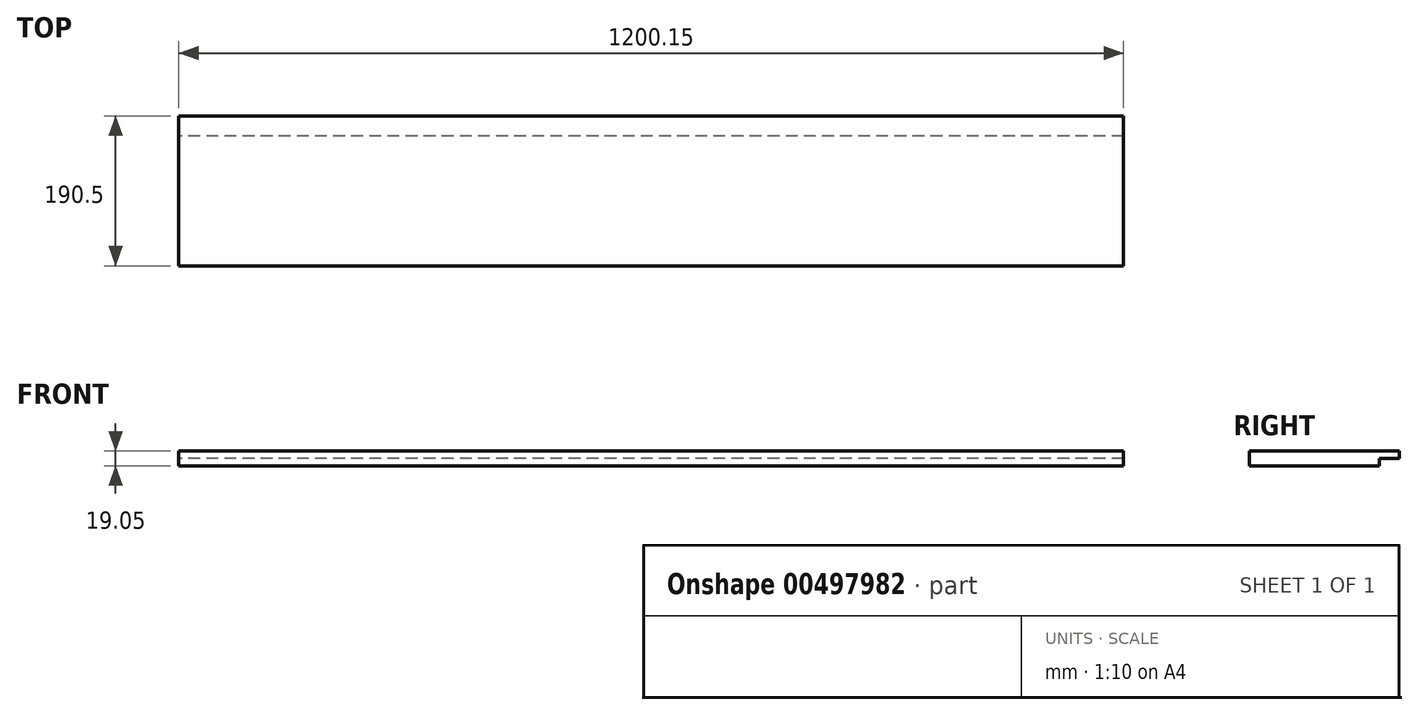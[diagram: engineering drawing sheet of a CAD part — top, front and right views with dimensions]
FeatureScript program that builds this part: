
annotation { "Feature Type Name" : "Feature", "Feature Type Description" : "" }
export const myFeature = defineFeature(function(context is Context, id is Id, definition is map)
    precondition{}
    {
        {
            var Q0;
            Q0=qCreatedBy(makeId("Right.planeOp"),FACE);
            var sketch = newSketch(context, id + "F0", { "sketchPlane" : qUnion([Q0])});
            skLineSegment(sketch, "E0.bottom", {"start": v(0, 0) * mm, "end": v(190.5, 0) * mm});
            skLineSegment(sketch, "E0.top", {"start": v(0, 19.05) * mm, "end": v(190.5, 19.05) * mm});
            skLineSegment(sketch, "E0.left", {"start": v(0, 0) * mm, "end": v(0, 19.05) * mm});
            skLineSegment(sketch, "E0.right", {"start": v(190.5, 0) * mm, "end": v(190.5, 19.05) * mm});
            skSolve(sketch);
        }
        {
            var Q0;
            Q0 = qSketchRegion(id + "F0", true);
            extrude(context, id + "F1", {"entities" : qUnion([Q0]), "depth" : 1200.15 * mm});
        }
        {
            var Q0;
            Q0=makeQuery(id+"F1.opExtrude","SWEPT_FACE",FACE,{"disambiguationData":[OSD([sQuery(id+"F0.wireOp",EDGE,"E0.right")])]});
            var sketch = newSketch(context, id + "F2", { "sketchPlane" : qUnion([Q0])});
            skLineSegment(sketch, "E1.0", {"start": v(-1200.15, 9.52) * mm, "end": v(0, 9.52) * mm});
            skSolve(sketch);
        }
        {
            var Q0;
            {var subQ0=sQuery(id+"F2.wireOp",EDGE,"E1.0");Q0=makeQuery(id+"F2.imprint","IMPRINT",FACE,{"disambiguationData":[TD([[makeQuery(id+"F2.imprint","IMPRINT",EDGE,{"derivedFrom":subQ0}),-1.0]])]});}
            extrude(context, id + "F3", {"entities" : qUnion([Q0]), "operationType" : NewBodyOperationType.REMOVE, "oppositeDirection" : true, "depth" : 25.4 * mm});
        }
    });
